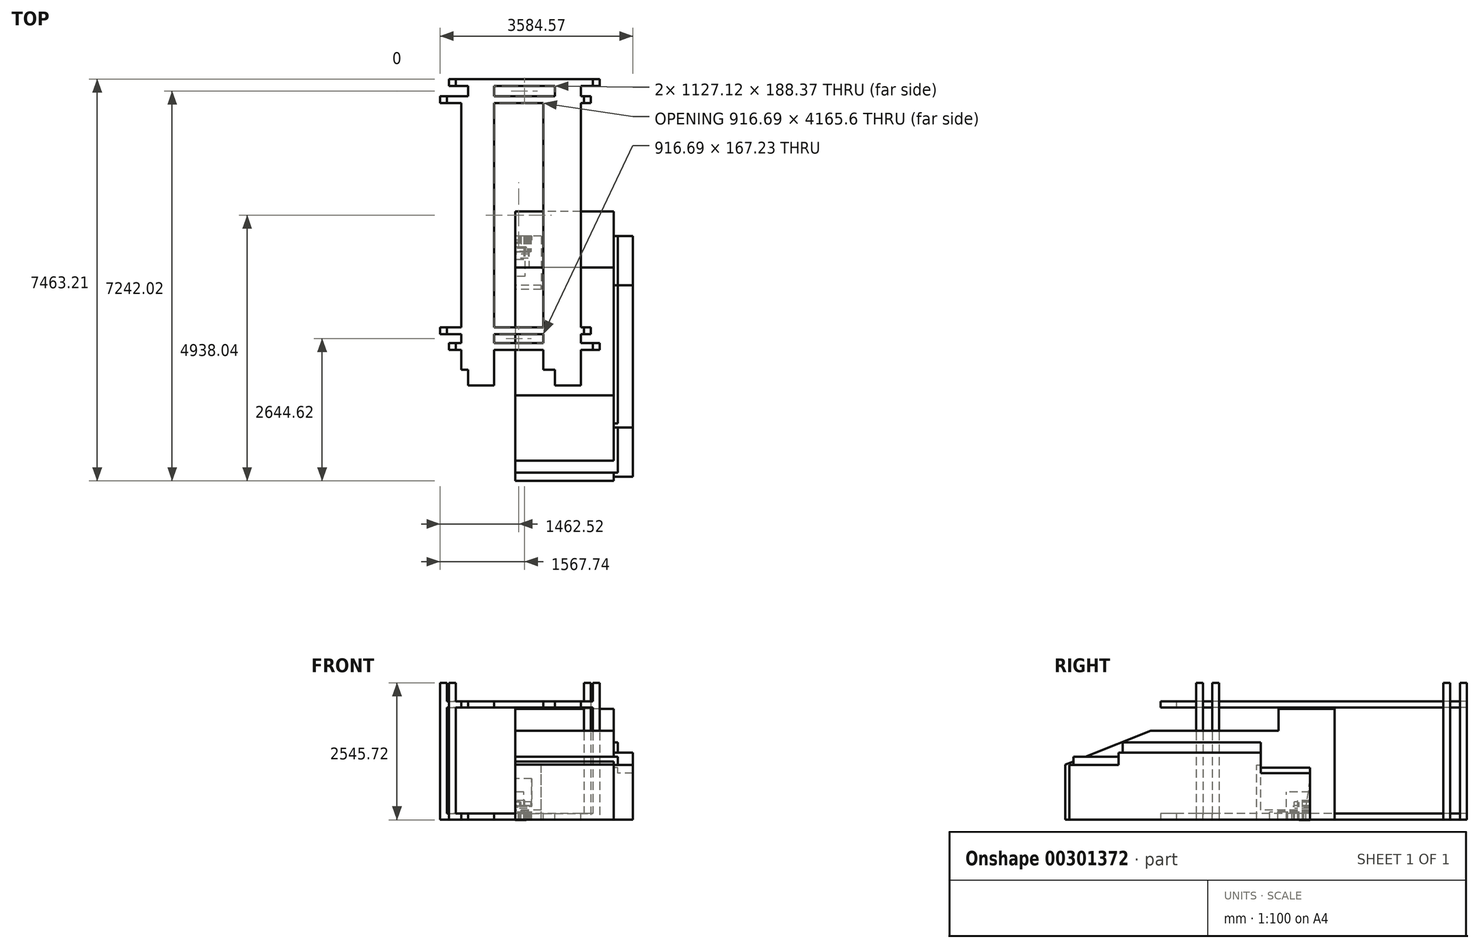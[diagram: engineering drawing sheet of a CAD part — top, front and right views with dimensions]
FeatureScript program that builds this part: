
annotation { "Feature Type Name" : "Feature", "Feature Type Description" : "" }
export const myFeature = defineFeature(function(context is Context, id is Id, definition is map)
    precondition{}
    {
        {
            var Q0;
            Q0=qCreatedBy(makeId("Right.planeOp"),FACE);
            var sketch = newSketch(context, id + "F0", { "sketchPlane" : qUnion([Q0])});
            skLineSegment(sketch, "E0.bottom", {"start": v(0, 0) * mm, "end": v(-4394.2, 0) * mm});
            skLineSegment(sketch, "E0.top", {"start": v(-914.4, 1435.1) * mm, "end": v(-3479.8, 1435.1) * mm});
            skLineSegment(sketch, "E0.left", {"start": v(0, 0) * mm, "end": v(0, 965.2) * mm});
            skLineSegment(sketch, "E0.right", {"start": v(-4394.2, 0) * mm, "end": v(-4394.2, 1168.4) * mm});
            skLineSegment(sketch, "E1", {"start": v(0, 965.2) * mm, "end": v(-914.4, 965.2) * mm});
            skLineSegment(sketch, "E2", {"start": v(-914.4, 965.2) * mm, "end": v(-914.4, 1435.1) * mm});
            skLineSegment(sketch, "E3", {"start": v(-4394.2, 1168.4) * mm, "end": v(-3479.8, 1168.4) * mm});
            skLineSegment(sketch, "E4", {"start": v(-3479.8, 1168.4) * mm, "end": v(-3479.8, 1435.1) * mm});
            skSolve(sketch);
        }
        {
            var Q0;
            Q0=makeQuery(id+"F0.imprint","IMPRINT",FACE,{"disambiguationData":[TD([[makeQuery(id+"F0.imprint","IMPRINT",EDGE,{"derivedFrom":sQuery(id+"F0.wireOp",EDGE,"E0.bottom")}),-1.0]])]});
            extrude(context, id + "F1", {"entities" : qUnion([Q0]), "depth" : 1905 * mm});
        }
        {
            var Q0;
            Q0=qCreatedBy(makeId("Right.planeOp"),FACE);
            var sketch = newSketch(context, id + "F2", { "sketchPlane" : qUnion([Q0])});
            skLineSegment(sketch, "E5.bottom", {"start": v(0, 0) * mm, "end": v(-4470.4, 0) * mm});
            skLineSegment(sketch, "E5.top", {"start": v(-914.4, 1244.6) * mm, "end": v(-3556, 1244.6) * mm});
            skLineSegment(sketch, "E5.left", {"start": v(0, 0) * mm, "end": v(0, 863.6) * mm});
            skLineSegment(sketch, "E5.right", {"start": v(-4470.4, 0) * mm, "end": v(-4470.4, 1016) * mm});
            skLineSegment(sketch, "E6.top", {"start": v(-4470.4, 1016) * mm, "end": v(-3556, 1016) * mm});
            skLineSegment(sketch, "E6.right", {"start": v(-3556, 1244.6) * mm, "end": v(-3556, 1016) * mm});
            skLineSegment(sketch, "E7.top", {"start": v(0, 863.6) * mm, "end": v(-914.4, 863.6) * mm});
            skLineSegment(sketch, "E7.right", {"start": v(-914.4, 1244.6) * mm, "end": v(-914.4, 863.6) * mm});
            skSolve(sketch);
        }
        {
            var Q0;
            Q0 = qSketchRegion(id + "F2", true);
            extrude(context, id + "F3", {"entities" : qUnion([Q0]), "depth" : 2184.4 * mm});
        }
        {
            var Q0;
            Q0=qCreatedBy(makeId("Right.planeOp"),FACE);
            var sketch = newSketch(context, id + "F4", { "sketchPlane" : qUnion([Q0])});
            skLineSegment(sketch, "E8.bottom", {"start": v(0, 0) * mm, "end": v(-990.6, 0) * mm});
            skLineSegment(sketch, "E8.top", {"start": v(0, 177.8) * mm, "end": v(-914.4, 177.8) * mm});
            skLineSegment(sketch, "E8.left", {"start": v(0, 0) * mm, "end": v(0, 177.8) * mm});
            skLineSegment(sketch, "E8.right", {"start": v(-990.6, 0) * mm, "end": v(-990.6, 177.8) * mm});
            skLineSegment(sketch, "E9.top", {"start": v(-990.6, 1016) * mm, "end": v(-914.4, 1016) * mm});
            skLineSegment(sketch, "E9.left", {"start": v(-990.6, 177.8) * mm, "end": v(-990.6, 1016) * mm});
            skLineSegment(sketch, "E9.right", {"start": v(-914.4, 177.8) * mm, "end": v(-914.4, 1016) * mm});
            skSolve(sketch);
        }
        {
            var Q0;
            Q0=makeQuery(id+"F4.imprint","IMPRINT",FACE,{"disambiguationData":[TD([[makeQuery(id+"F4.imprint","IMPRINT",EDGE,{"derivedFrom":sQuery(id+"F4.wireOp",EDGE,"E8.bottom")}),-1.0]])]});
            extrude(context, id + "F5", {"entities" : qUnion([Q0]), "depth" : 482.6 * mm});
        }
        {
            var Q0;
            Q0=qCreatedBy(makeId("Right.planeOp"),FACE);
            var sketch = newSketch(context, id + "F6", { "sketchPlane" : qUnion([Q0])});
            skLineSegment(sketch, "E10.bottom", {"start": v(0, 0) * mm, "end": v(-596.9, 0) * mm});
            skLineSegment(sketch, "E10.top", {"start": v(0, 165.1) * mm, "end": v(-596.9, 165.1) * mm});
            skLineSegment(sketch, "E10.left", {"start": v(0, 0) * mm, "end": v(0, 165.1) * mm});
            skLineSegment(sketch, "E10.right", {"start": v(-596.9, 0) * mm, "end": v(-596.9, 165.1) * mm});
            skSolve(sketch);
        }
        {
            var Q0;
            Q0=makeQuery(id+"F6.imprint","IMPRINT",FACE,{"disambiguationData":[TD([[makeQuery(id+"F6.imprint","IMPRINT",EDGE,{"derivedFrom":sQuery(id+"F6.wireOp",EDGE,"E10.bottom")}),-1.0]])]});
            extrude(context, id + "F7", {"entities" : qUnion([Q0]), "depth" : 254 * mm});
        }
        {
            var Q0;
            Q0=qCreatedBy(makeId("Right.planeOp"),FACE);
            var sketch = newSketch(context, id + "F8", { "sketchPlane" : qUnion([Q0])});
            skLineSegment(sketch, "E11.bottom", {"start": v(0, 0) * mm, "end": v(-228.6, 0) * mm});
            skLineSegment(sketch, "E11.top", {"start": v(0, 355.6) * mm, "end": v(-228.6, 355.6) * mm});
            skLineSegment(sketch, "E11.left", {"start": v(0, 0) * mm, "end": v(0, 355.6) * mm});
            skLineSegment(sketch, "E11.right", {"start": v(-228.6, 0) * mm, "end": v(-228.6, 355.6) * mm});
            skSolve(sketch);
        }
        {
            var Q0;
            Q0 = qSketchRegion(id + "F8", true);
            extrude(context, id + "F9", {"entities" : qUnion([Q0]), "depth" : 177.8 * mm});
        }
        {
            var Q0;
            Q0=qCreatedBy(makeId("Right.planeOp"),FACE);
            var sketch = newSketch(context, id + "F10", { "sketchPlane" : qUnion([Q0])});
            skLineSegment(sketch, "E12.bottom", {"start": v(0, 0) * mm, "end": v(-215.9, 0) * mm});
            skLineSegment(sketch, "E12.top", {"start": v(0, 241.3) * mm, "end": v(-215.9, 241.3) * mm});
            skLineSegment(sketch, "E12.left", {"start": v(0, 0) * mm, "end": v(0, 241.3) * mm});
            skLineSegment(sketch, "E12.right", {"start": v(-215.9, 0) * mm, "end": v(-215.9, 241.3) * mm});
            skSolve(sketch);
        }
        {
            var Q0;
            Q0 = qSketchRegion(id + "F10", true);
            extrude(context, id + "F11", {"entities" : qUnion([Q0]), "depth" : 215.9 * mm});
        }
        {
            var Q0;
            Q0=qCreatedBy(makeId("Right.planeOp"),FACE);
            var sketch = newSketch(context, id + "F12", { "sketchPlane" : qUnion([Q0])});
            skLineSegment(sketch, "E13.bottom", {"start": v(0, 0) * mm, "end": v(-76.2, 0) * mm});
            skLineSegment(sketch, "E13.left", {"start": v(0, 0) * mm, "end": v(0, 762) * mm});
            skLineSegment(sketch, "E13.right", {"start": v(-76.2, 0) * mm, "end": v(-76.2, 254) * mm});
            skLineSegment(sketch, "E14", {"start": v(0, 762) * mm, "end": v(-76.2, 254) * mm});
            skSolve(sketch);
        }
        {
            var Q0;
            Q0 = qSketchRegion(id + "F12", true);
            extrude(context, id + "F13", {"entities" : qUnion([Q0]), "depth" : 304.8 * mm});
        }
        {
            var Q0;
            Q0=qCreatedBy(makeId("Right.planeOp"),FACE);
            var sketch = newSketch(context, id + "F14", { "sketchPlane" : qUnion([Q0])});
            skLineSegment(sketch, "E15.bottom", {"start": v(0, -5.72) * mm, "end": v(-203.2, -5.72) * mm});
            skLineSegment(sketch, "E15.top", {"start": v(0, 133.98) * mm, "end": v(-203.2, 133.98) * mm});
            skLineSegment(sketch, "E15.left", {"start": v(0, -5.72) * mm, "end": v(0, 133.98) * mm});
            skLineSegment(sketch, "E15.right", {"start": v(-203.2, -5.72) * mm, "end": v(-203.2, 133.98) * mm});
            skSolve(sketch);
        }
        {
            var Q0;
            Q0=makeQuery(id+"F14.imprint","IMPRINT",FACE,{"disambiguationData":[TD([[makeQuery(id+"F14.imprint","IMPRINT",EDGE,{"derivedFrom":sQuery(id+"F14.wireOp",EDGE,"E15.bottom")}),-1.0]])]});
            extrude(context, id + "F15", {"entities" : qUnion([Q0]), "depth" : 203.2 * mm});
        }
        {
            var Q0;
            Q0=qCreatedBy(makeId("Right.planeOp"),FACE);
            var sketch = newSketch(context, id + "F16", { "sketchPlane" : qUnion([Q0])});
            skLineSegment(sketch, "E16.bottom", {"start": v(0, 0) * mm, "end": v(-749.3, 0) * mm});
            skLineSegment(sketch, "E16.top", {"start": v(0, 139.7) * mm, "end": v(-749.3, 139.7) * mm});
            skLineSegment(sketch, "E16.left", {"start": v(0, 0) * mm, "end": v(0, 139.7) * mm});
            skLineSegment(sketch, "E16.right", {"start": v(-749.3, 0) * mm, "end": v(-749.3, 139.7) * mm});
            skSolve(sketch);
        }
        {
            var Q0;
            Q0 = qSketchRegion(id + "F16", true);
            extrude(context, id + "F17", {"entities" : qUnion([Q0]), "depth" : 177.8 * mm});
        }
        {
            var Q0;
            Q0=qCreatedBy(makeId("Right.planeOp"),FACE);
            var sketch = newSketch(context, id + "F18", { "sketchPlane" : qUnion([Q0])});
            skLineSegment(sketch, "E17.bottom", {"start": v(0, 0) * mm, "end": v(-336.55, 0) * mm});
            skLineSegment(sketch, "E17.top", {"start": v(0, 114.3) * mm, "end": v(-336.55, 114.3) * mm});
            skLineSegment(sketch, "E17.left", {"start": v(0, 0) * mm, "end": v(0, 114.3) * mm});
            skLineSegment(sketch, "E17.right", {"start": v(-336.55, 0) * mm, "end": v(-336.55, 114.3) * mm});
            skSolve(sketch);
        }
        {
            var Q0;
            Q0 = qSketchRegion(id + "F18", true);
            extrude(context, id + "F19", {"entities" : qUnion([Q0]), "depth" : 254 * mm});
        }
        {
            var Q0;
            Q0=qCreatedBy(makeId("Right.planeOp"),FACE);
            var sketch = newSketch(context, id + "F20", { "sketchPlane" : qUnion([Q0])});
            skLineSegment(sketch, "E18.bottom", {"start": v(0, 0) * mm, "end": v(-285.75, 0) * mm});
            skLineSegment(sketch, "E18.top", {"start": v(0, 209.55) * mm, "end": v(-285.75, 209.55) * mm});
            skLineSegment(sketch, "E18.left", {"start": v(0, 0) * mm, "end": v(0, 209.55) * mm});
            skLineSegment(sketch, "E18.right", {"start": v(-285.75, 0) * mm, "end": v(-285.75, 209.55) * mm});
            skSolve(sketch);
        }
        {
            var Q0;
            Q0 = qSketchRegion(id + "F20", true);
            extrude(context, id + "F21", {"entities" : qUnion([Q0]), "depth" : 222.25 * mm});
        }
        {
            var Q0;
            Q0=qCreatedBy(makeId("Right.planeOp"),FACE);
            var sketch = newSketch(context, id + "F22", { "sketchPlane" : qUnion([Q0])});
            skLineSegment(sketch, "E19.bottom", {"start": v(0, 0) * mm, "end": v(-298.45, 0) * mm});
            skLineSegment(sketch, "E19.top", {"start": v(0, 139.7) * mm, "end": v(-298.45, 139.7) * mm});
            skLineSegment(sketch, "E19.left", {"start": v(0, 0) * mm, "end": v(0, 139.7) * mm});
            skLineSegment(sketch, "E19.right", {"start": v(-298.45, 0) * mm, "end": v(-298.45, 139.7) * mm});
            skSolve(sketch);
        }
        {
            var Q0;
            Q0 = qSketchRegion(id + "F22", true);
            extrude(context, id + "F23", {"entities" : qUnion([Q0]), "depth" : 190.5 * mm});
        }
        {
            var Q0;
            Q0=qCreatedBy(makeId("Right.planeOp"),FACE);
            var sketch = newSketch(context, id + "F24", { "sketchPlane" : qUnion([Q0])});
            skLineSegment(sketch, "E20.bottom", {"start": v(0, 0) * mm, "end": v(-412.75, 0) * mm});
            skLineSegment(sketch, "E20.top", {"start": v(0, 165.1) * mm, "end": v(-412.75, 165.1) * mm});
            skLineSegment(sketch, "E20.left", {"start": v(0, 0) * mm, "end": v(0, 165.1) * mm});
            skLineSegment(sketch, "E20.right", {"start": v(-412.75, 0) * mm, "end": v(-412.75, 165.1) * mm});
            skSolve(sketch);
        }
        {
            var Q0;
            Q0 = qSketchRegion(id + "F24", true);
            extrude(context, id + "F25", {"entities" : qUnion([Q0]), "depth" : 241.3 * mm});
        }
        {
            var Q0;
            Q0=qCreatedBy(makeId("Right.planeOp"),FACE);
            var sketch = newSketch(context, id + "F26", { "sketchPlane" : qUnion([Q0])});
            skLineSegment(sketch, "E21.bottom", {"start": v(0, 0) * mm, "end": v(-139.7, 0) * mm});
            skLineSegment(sketch, "E21.top", {"start": v(0, 336.55) * mm, "end": v(-139.7, 336.55) * mm});
            skLineSegment(sketch, "E21.left", {"start": v(0, 0) * mm, "end": v(0, 336.55) * mm});
            skLineSegment(sketch, "E21.right", {"start": v(-139.7, 0) * mm, "end": v(-139.7, 336.55) * mm});
            skSolve(sketch);
        }
        {
            var Q0;
            Q0 = qSketchRegion(id + "F26", true);
            extrude(context, id + "F27", {"entities" : qUnion([Q0]), "depth" : 82.55 * mm});
        }
        {
            var Q0;
            Q0=qCreatedBy(makeId("Right.planeOp"),FACE);
            var sketch = newSketch(context, id + "F28", { "sketchPlane" : qUnion([Q0])});
            skLineSegment(sketch, "E22.bottom", {"start": v(0, 0) * mm, "end": v(-304.8, 0) * mm});
            skLineSegment(sketch, "E22.top", {"start": v(0, 260.35) * mm, "end": v(-304.8, 260.35) * mm});
            skLineSegment(sketch, "E22.left", {"start": v(0, 0) * mm, "end": v(0, 260.35) * mm});
            skLineSegment(sketch, "E22.right", {"start": v(-304.8, 0) * mm, "end": v(-304.8, 260.35) * mm});
            skSolve(sketch);
        }
        {
            var Q0;
            Q0 = qSketchRegion(id + "F28", true);
            extrude(context, id + "F29", {"entities" : qUnion([Q0]), "depth" : 266.7 * mm});
        }
        {
            var Q0;
            Q0=qCreatedBy(makeId("Right.planeOp"),FACE);
            var sketch = newSketch(context, id + "F30", { "sketchPlane" : qUnion([Q0])});
            skLineSegment(sketch, "E23.bottom", {"start": v(0, 0) * mm, "end": v(-438.15, 0) * mm});
            skLineSegment(sketch, "E23.top", {"start": v(0, 514.35) * mm, "end": v(-438.15, 514.35) * mm});
            skLineSegment(sketch, "E23.left", {"start": v(0, 0) * mm, "end": v(0, 514.35) * mm});
            skLineSegment(sketch, "E23.right", {"start": v(-438.15, 0) * mm, "end": v(-438.15, 514.35) * mm});
            skSolve(sketch);
        }
        {
            var Q0;
            Q0 = qSketchRegion(id + "F30", true);
            extrude(context, id + "F31", {"entities" : qUnion([Q0]), "depth" : 158.75 * mm});
        }
        {
            var Q0;
            Q0=qCreatedBy(makeId("Right.planeOp"),FACE);
            var sketch = newSketch(context, id + "F32", { "sketchPlane" : qUnion([Q0])});
            skLineSegment(sketch, "E24.bottom", {"start": v(0, 0) * mm, "end": v(-203.2, 0) * mm});
            skLineSegment(sketch, "E24.top", {"start": v(0, 323.85) * mm, "end": v(-203.2, 323.85) * mm});
            skLineSegment(sketch, "E24.left", {"start": v(0, 0) * mm, "end": v(0, 323.85) * mm});
            skLineSegment(sketch, "E24.right", {"start": v(-203.2, 0) * mm, "end": v(-203.2, 323.85) * mm});
            skSolve(sketch);
        }
        {
            var Q0;
            Q0 = qSketchRegion(id + "F32", true);
            extrude(context, id + "F33", {"entities" : qUnion([Q0]), "depth" : 107.95 * mm});
        }
        {
            var Q0;
            Q0=qCreatedBy(makeId("Right.planeOp"),FACE);
            var sketch = newSketch(context, id + "F34", { "sketchPlane" : qUnion([Q0])});
            skLineSegment(sketch, "E25.bottom", {"start": v(0, 0) * mm, "end": v(-114.3, 0) * mm});
            skLineSegment(sketch, "E25.top", {"start": v(0, 228.6) * mm, "end": v(-114.3, 228.6) * mm});
            skLineSegment(sketch, "E25.left", {"start": v(0, 0) * mm, "end": v(0, 228.6) * mm});
            skLineSegment(sketch, "E25.right", {"start": v(-114.3, 0) * mm, "end": v(-114.3, 228.6) * mm});
            skSolve(sketch);
        }
        {
            var Q0;
            Q0 = qSketchRegion(id + "F34", true);
            extrude(context, id + "F35", {"entities" : qUnion([Q0]), "depth" : 57.15 * mm});
        }
        {
            var Q0;
            Q0=qCreatedBy(makeId("Right.planeOp"),FACE);
            var sketch = newSketch(context, id + "F36", { "sketchPlane" : qUnion([Q0])});
            skLineSegment(sketch, "E26.bottom", {"start": v(0, 0) * mm, "end": v(-292.1, 0) * mm});
            skLineSegment(sketch, "E26.top", {"start": v(0, 330.2) * mm, "end": v(-292.1, 330.2) * mm});
            skLineSegment(sketch, "E26.left", {"start": v(0, 0) * mm, "end": v(0, 330.2) * mm});
            skLineSegment(sketch, "E26.right", {"start": v(-292.1, 0) * mm, "end": v(-292.1, 330.2) * mm});
            skSolve(sketch);
        }
        {
            var Q0;
            Q0 = qSketchRegion(id + "F36", true);
            extrude(context, id + "F37", {"entities" : qUnion([Q0]), "depth" : 292.1 * mm});
        }
        {
            var Q0;
            Q0=qCreatedBy(makeId("Right.planeOp"),FACE);
            var sketch = newSketch(context, id + "F38", { "sketchPlane" : qUnion([Q0])});
            skLineSegment(sketch, "E27.bottom", {"start": v(0, 0) * mm, "end": v(-4546.6, 0) * mm});
            skLineSegment(sketch, "E27.top", {"start": v(-583.6, 1651) * mm, "end": v(-2956.24, 1651) * mm});
            skLineSegment(sketch, "E27.left", {"start": v(0, 0) * mm, "end": v(0, 825.5) * mm});
            skLineSegment(sketch, "E27.right", {"start": v(-4546.6, 0) * mm, "end": v(-4546.6, 1018.82) * mm});
            skLineSegment(sketch, "E28", {"start": v(-2956.24, 1651) * mm, "end": v(-4546.6, 1018.82) * mm});
            skLineSegment(sketch, "E29", {"start": v(-583.6, 1651) * mm, "end": v(0, 825.5) * mm});
            skPoint(sketch, "E30.orphan", {"position": v(0, 1651) * mm});
            skLineSegment(sketch, "E31", {"start": v(-583.6, 2057.4) * mm, "end": v(457.2, 2057.4) * mm});
            skLineSegment(sketch, "E32", {"start": v(457.2, 0) * mm, "end": v(457.2, 2057.4) * mm});
            skLineSegment(sketch, "E33", {"start": v(-583.6, 1651) * mm, "end": v(-583.6, 2057.4) * mm});
            skLineSegment(sketch, "E34", {"start": v(457.2, 0) * mm, "end": v(0, 0) * mm});
            skSolve(sketch);
        }
        {
            var Q0;
            Q0 = qSketchRegion(id + "F38", true);
            extrude(context, id + "F39", {"entities" : qUnion([Q0]), "depth" : 1828.8 * mm});
        }
        {
            var Q0;
            Q0=qCreatedBy(makeId("Top.planeOp"),FACE);
            var sketch = newSketch(context, id + "F40", { "sketchPlane" : qUnion([Q0])});
            skLineSegment(sketch, "E35.bottom", {"start": v(1440.75, 2916.6) * mm, "end": v(1567.75, 2916.6) * mm});
            skLineSegment(sketch, "E35.top", {"start": v(1440.75, 2789.6) * mm, "end": v(1567.75, 2789.6) * mm});
            skLineSegment(sketch, "E35.left", {"start": v(1440.75, 2916.6) * mm, "end": v(1440.75, 2789.6) * mm});
            skLineSegment(sketch, "E35.right", {"start": v(1567.75, 2916.6) * mm, "end": v(1567.75, 2789.6) * mm});
            skLineSegment(sketch, "E36.bottom", {"start": v(1567.75, -1985.6) * mm, "end": v(1440.75, -1985.6) * mm});
            skLineSegment(sketch, "E36.top", {"start": v(1567.75, -2112.6) * mm, "end": v(1440.75, -2112.6) * mm});
            skLineSegment(sketch, "E36.left", {"start": v(1567.75, -1985.6) * mm, "end": v(1567.75, -2112.6) * mm});
            skLineSegment(sketch, "E36.right", {"start": v(1440.75, -1985.6) * mm, "end": v(1440.75, -2112.6) * mm});
            skLineSegment(sketch, "E37", {"start": v(167.57, 3036.9) * mm, "end": v(167.57, -1974.98) * mm, "construction": true});
            skLineSegment(sketch, "E38.bottom", {"start": v(1213.73, 2916.6) * mm, "end": v(731.13, 2916.6) * mm});
            skLineSegment(sketch, "E38.top", {"start": v(1213.73, -2773) * mm, "end": v(731.13, -2773) * mm});
            skLineSegment(sketch, "E38.left", {"start": v(1213.73, 2916.6) * mm, "end": v(1213.73, -2773) * mm});
            skLineSegment(sketch, "E38.right", {"start": v(731.13, 2916.6) * mm, "end": v(731.13, -2773) * mm});
            skLineSegment(sketch, "E39.MirrorCS", {"start": v(-878.6, -2773) * mm, "end": v(-396, -2773) * mm});
            skLineSegment(sketch, "E40.MirrorCS", {"start": v(-396, 2916.6) * mm, "end": v(-396, -2773) * mm});
            skLineSegment(sketch, "E41.MirrorCS", {"start": v(-878.6, 2916.6) * mm, "end": v(-878.6, -2773) * mm});
            skLineSegment(sketch, "E42.MirrorCS", {"start": v(-878.6, 2916.6) * mm, "end": v(-396, 2916.6) * mm});
            skLineSegment(sketch, "E43.MirrorCS", {"start": v(-1105.6, 2916.6) * mm, "end": v(-1105.6, 2789.6) * mm});
            skLineSegment(sketch, "E44.MirrorCS", {"start": v(-1232.6, 2916.6) * mm, "end": v(-1232.6, 2789.6) * mm});
            skLineSegment(sketch, "E45.MirrorCS", {"start": v(-1105.6, 2789.6) * mm, "end": v(-1232.6, 2789.6) * mm});
            skLineSegment(sketch, "E46.MirrorCS", {"start": v(-1105.6, 2916.6) * mm, "end": v(-1232.6, 2916.6) * mm});
            skLineSegment(sketch, "E47.MirrorCS", {"start": v(-1232.6, -1985.6) * mm, "end": v(-1232.6, -2112.6) * mm});
            skLineSegment(sketch, "E48.MirrorCS", {"start": v(-1232.6, -1985.6) * mm, "end": v(-1105.6, -1985.6) * mm});
            skLineSegment(sketch, "E49.MirrorCS", {"start": v(-1105.6, -1985.6) * mm, "end": v(-1105.6, -2112.6) * mm});
            skLineSegment(sketch, "E50.MirrorCS", {"start": v(-1232.6, -2112.6) * mm, "end": v(-1105.6, -2112.6) * mm});
            skLineSegment(sketch, "E51", {"start": v(-1105.6, 2916.6) * mm, "end": v(1440.75, 2916.6) * mm});
            skLineSegment(sketch, "E52", {"start": v(1440.75, 2789.6) * mm, "end": v(-1105.6, 2789.6) * mm});
            skLineSegment(sketch, "E53", {"start": v(1440.75, -1985.6) * mm, "end": v(-1105.6, -1985.6) * mm});
            skLineSegment(sketch, "E54", {"start": v(-1105.6, -2112.6) * mm, "end": v(1440.75, -2112.6) * mm});
            skSolve(sketch);
        }
        {
            var Q0;
            {var subQ0=sQuery(id+"F40.wireOp",EDGE,"E36.right");Q0=makeQuery(id+"F40.imprint","IMPRINT",FACE,{"disambiguationData":[TD([[makeQuery(id+"F40.imprint","IMPRINT",EDGE,{"derivedFrom":subQ0}),-1.0]])]});}
            var Q1;
            {var subQ0=sQuery(id+"F40.wireOp",EDGE,"E53");var subQ1=sQuery(id+"F40.wireOp",EDGE,"E38.left");var subQ2=makeQuery(id+"F40.imprint","INTERSECT",VERTEX,{"derivedFrom":[subQ1,subQ0]});Q1=makeQuery(id+"F40.imprint","IMPRINT",FACE,{"disambiguationData":[TD([[makeQuery(id+"F40.imprint","IMPRINT",EDGE,{"disambiguationData":[TD([[subQ2,-1.0]])],"derivedFrom":subQ1}),-1.0]])]});}
            var Q2;
            {var subQ0=sQuery(id+"F40.wireOp",EDGE,"E54");var subQ1=sQuery(id+"F40.wireOp",EDGE,"E38.right");var subQ2=makeQuery(id+"F40.imprint","INTERSECT",VERTEX,{"derivedFrom":[subQ1,subQ0]});Q2=makeQuery(id+"F40.imprint","IMPRINT",FACE,{"disambiguationData":[TD([[makeQuery(id+"F40.imprint","IMPRINT",EDGE,{"disambiguationData":[TD([[subQ2,1.0]])],"derivedFrom":subQ1}),-1.0]])]});}
            var Q3;
            {var subQ0=sQuery(id+"F40.wireOp",EDGE,"E54");var subQ1=sQuery(id+"F40.wireOp",EDGE,"E40.MirrorCS");var subQ2=makeQuery(id+"F40.imprint","INTERSECT",VERTEX,{"derivedFrom":[subQ1,subQ0]});Q3=makeQuery(id+"F40.imprint","IMPRINT",FACE,{"disambiguationData":[TD([[makeQuery(id+"F40.imprint","IMPRINT",EDGE,{"disambiguationData":[TD([[subQ2,1.0]])],"derivedFrom":subQ1}),-1.0]])]});}
            var Q4;
            {var subQ5=sQuery(id+"F40.wireOp",EDGE,"E49.MirrorCS");Q4=makeQuery(id+"F40.imprint","IMPRINT",FACE,{"disambiguationData":[TD([[makeQuery(id+"F40.imprint","IMPRINT",EDGE,{"derivedFrom":subQ5}),1.0]])]});}
            var Q5;
            {var subQ0=sQuery(id+"F40.wireOp",EDGE,"E52");var subQ1=sQuery(id+"F40.wireOp",EDGE,"E40.MirrorCS");var subQ2=makeQuery(id+"F40.imprint","INTERSECT",VERTEX,{"derivedFrom":[subQ1,subQ0]});Q5=makeQuery(id+"F40.imprint","IMPRINT",FACE,{"disambiguationData":[TD([[makeQuery(id+"F40.imprint","IMPRINT",EDGE,{"disambiguationData":[TD([[subQ2,-1.0]])],"derivedFrom":subQ1}),-1.0]])]});}
            var Q6;
            {var subQ0=sQuery(id+"F40.wireOp",EDGE,"E39.MirrorCS");Q6=makeQuery(id+"F40.imprint","IMPRINT",FACE,{"disambiguationData":[TD([[makeQuery(id+"F40.imprint","IMPRINT",EDGE,{"derivedFrom":subQ0}),1.0]])]});}
            var Q7;
            {var subQ0=sQuery(id+"F40.wireOp",EDGE,"E38.top");Q7=makeQuery(id+"F40.imprint","IMPRINT",FACE,{"disambiguationData":[TD([[makeQuery(id+"F40.imprint","IMPRINT",EDGE,{"derivedFrom":subQ0}),-1.0]])]});}
            var Q8;
            {var subQ0=sQuery(id+"F40.wireOp",EDGE,"E52");var subQ1=sQuery(id+"F40.wireOp",EDGE,"E38.left");var subQ2=makeQuery(id+"F40.imprint","INTERSECT",VERTEX,{"derivedFrom":[subQ1,subQ0]});Q8=makeQuery(id+"F40.imprint","IMPRINT",FACE,{"disambiguationData":[TD([[makeQuery(id+"F40.imprint","IMPRINT",EDGE,{"disambiguationData":[TD([[subQ2,-1.0]])],"derivedFrom":subQ1}),-1.0]])]});}
            var Q9;
            {var subQ0=sQuery(id+"F40.wireOp",EDGE,"E35.left");Q9=makeQuery(id+"F40.imprint","IMPRINT",FACE,{"disambiguationData":[TD([[makeQuery(id+"F40.imprint","IMPRINT",EDGE,{"derivedFrom":subQ0}),-1.0]])]});}
            var Q10;
            {var subQ0=sQuery(id+"F40.wireOp",EDGE,"E51");var subQ1=sQuery(id+"F40.wireOp",EDGE,"E38.left");var subQ2=makeQuery(id+"F40.imprint","INTERSECT",VERTEX,{"derivedFrom":[subQ1,subQ0]});Q10=makeQuery(id+"F40.imprint","IMPRINT",FACE,{"disambiguationData":[TD([[makeQuery(id+"F40.imprint","IMPRINT",EDGE,{"disambiguationData":[TD([[subQ2,-1.0]])],"derivedFrom":subQ1}),-1.0]])]});}
            var Q11;
            {var subQ0=sQuery(id+"F40.wireOp",EDGE,"E51");var subQ1=sQuery(id+"F40.wireOp",EDGE,"E38.right");var subQ2=makeQuery(id+"F40.imprint","INTERSECT",VERTEX,{"derivedFrom":[subQ1,subQ0]});Q11=makeQuery(id+"F40.imprint","IMPRINT",FACE,{"disambiguationData":[TD([[makeQuery(id+"F40.imprint","IMPRINT",EDGE,{"disambiguationData":[TD([[subQ2,-1.0]])],"derivedFrom":subQ1}),-1.0]])]});}
            var Q12;
            {var subQ0=sQuery(id+"F40.wireOp",EDGE,"E51");var subQ1=sQuery(id+"F40.wireOp",EDGE,"E40.MirrorCS");var subQ2=makeQuery(id+"F40.imprint","INTERSECT",VERTEX,{"derivedFrom":[subQ1,subQ0]});Q12=makeQuery(id+"F40.imprint","IMPRINT",FACE,{"disambiguationData":[TD([[makeQuery(id+"F40.imprint","IMPRINT",EDGE,{"disambiguationData":[TD([[subQ2,-1.0]])],"derivedFrom":subQ1}),-1.0]])]});}
            var Q13;
            {var subQ5=sQuery(id+"F40.wireOp",EDGE,"E43.MirrorCS");Q13=makeQuery(id+"F40.imprint","IMPRINT",FACE,{"disambiguationData":[TD([[makeQuery(id+"F40.imprint","IMPRINT",EDGE,{"derivedFrom":subQ5}),1.0]])]});}
            extrude(context, id + "F41", {"entities" : qUnion([Q0, Q1, Q2, Q3, Q4, Q5, Q6, Q7, Q8, Q9, Q10, Q11, Q12, Q13]), "depth" : 2197.1 * mm, "hasSecondDirection" : true, "secondDirectionOppositeDirection" : false, "secondDirectionDepth" : 2082.8 * mm});
        }
        {
            var Q0;
            Q0=makeQuery(id+"F40.imprint","IMPRINT",FACE,{"disambiguationData":[TD([[makeQuery(id+"F40.imprint","IMPRINT",EDGE,{"derivedFrom":sQuery(id+"F40.wireOp",EDGE,"E47.MirrorCS")}),1.0]])]});
            var Q1;
            Q1=makeQuery(id+"F40.imprint","IMPRINT",FACE,{"disambiguationData":[TD([[makeQuery(id+"F40.imprint","IMPRINT",EDGE,{"derivedFrom":sQuery(id+"F40.wireOp",EDGE,"E36.bottom")}),1.0]])]});
            var Q2;
            Q2=makeQuery(id+"F40.imprint","IMPRINT",FACE,{"disambiguationData":[TD([[makeQuery(id+"F40.imprint","IMPRINT",EDGE,{"derivedFrom":sQuery(id+"F40.wireOp",EDGE,"E35.bottom")}),-1.0]])]});
            var Q3;
            Q3=makeQuery(id+"F40.imprint","IMPRINT",FACE,{"disambiguationData":[TD([[makeQuery(id+"F40.imprint","IMPRINT",EDGE,{"derivedFrom":sQuery(id+"F40.wireOp",EDGE,"E43.MirrorCS")}),-1.0]])]});
            extrude(context, id + "F42", {"entities" : qUnion([Q0, Q1, Q2, Q3]), "operationType" : NewBodyOperationType.ADD, "depth" : 2540 * mm});
        }
        {
            var Q0;
            {var subQ5=sQuery(id+"F40.wireOp",EDGE,"E49.MirrorCS");Q0=makeQuery(id+"F40.imprint","IMPRINT",FACE,{"disambiguationData":[TD([[makeQuery(id+"F40.imprint","IMPRINT",EDGE,{"derivedFrom":subQ5}),1.0]])]});}
            var Q1;
            {var subQ0=sQuery(id+"F40.wireOp",EDGE,"E39.MirrorCS");Q1=makeQuery(id+"F40.imprint","IMPRINT",FACE,{"disambiguationData":[TD([[makeQuery(id+"F40.imprint","IMPRINT",EDGE,{"derivedFrom":subQ0}),1.0]])]});}
            var Q2;
            {var subQ0=sQuery(id+"F40.wireOp",EDGE,"E54");var subQ1=sQuery(id+"F40.wireOp",EDGE,"E40.MirrorCS");var subQ2=makeQuery(id+"F40.imprint","INTERSECT",VERTEX,{"derivedFrom":[subQ1,subQ0]});Q2=makeQuery(id+"F40.imprint","IMPRINT",FACE,{"disambiguationData":[TD([[makeQuery(id+"F40.imprint","IMPRINT",EDGE,{"disambiguationData":[TD([[subQ2,1.0]])],"derivedFrom":subQ1}),-1.0]])]});}
            var Q3;
            {var subQ0=sQuery(id+"F40.wireOp",EDGE,"E52");var subQ1=sQuery(id+"F40.wireOp",EDGE,"E40.MirrorCS");var subQ2=makeQuery(id+"F40.imprint","INTERSECT",VERTEX,{"derivedFrom":[subQ1,subQ0]});Q3=makeQuery(id+"F40.imprint","IMPRINT",FACE,{"disambiguationData":[TD([[makeQuery(id+"F40.imprint","IMPRINT",EDGE,{"disambiguationData":[TD([[subQ2,-1.0]])],"derivedFrom":subQ1}),-1.0]])]});}
            var Q4;
            {var subQ0=sQuery(id+"F40.wireOp",EDGE,"E54");var subQ1=sQuery(id+"F40.wireOp",EDGE,"E38.right");var subQ2=makeQuery(id+"F40.imprint","INTERSECT",VERTEX,{"derivedFrom":[subQ1,subQ0]});Q4=makeQuery(id+"F40.imprint","IMPRINT",FACE,{"disambiguationData":[TD([[makeQuery(id+"F40.imprint","IMPRINT",EDGE,{"disambiguationData":[TD([[subQ2,1.0]])],"derivedFrom":subQ1}),-1.0]])]});}
            var Q5;
            {var subQ0=sQuery(id+"F40.wireOp",EDGE,"E38.top");Q5=makeQuery(id+"F40.imprint","IMPRINT",FACE,{"disambiguationData":[TD([[makeQuery(id+"F40.imprint","IMPRINT",EDGE,{"derivedFrom":subQ0}),-1.0]])]});}
            var Q6;
            {var subQ0=sQuery(id+"F40.wireOp",EDGE,"E53");var subQ1=sQuery(id+"F40.wireOp",EDGE,"E38.left");var subQ2=makeQuery(id+"F40.imprint","INTERSECT",VERTEX,{"derivedFrom":[subQ1,subQ0]});Q6=makeQuery(id+"F40.imprint","IMPRINT",FACE,{"disambiguationData":[TD([[makeQuery(id+"F40.imprint","IMPRINT",EDGE,{"disambiguationData":[TD([[subQ2,-1.0]])],"derivedFrom":subQ1}),-1.0]])]});}
            var Q7;
            {var subQ0=sQuery(id+"F40.wireOp",EDGE,"E36.right");Q7=makeQuery(id+"F40.imprint","IMPRINT",FACE,{"disambiguationData":[TD([[makeQuery(id+"F40.imprint","IMPRINT",EDGE,{"derivedFrom":subQ0}),-1.0]])]});}
            var Q8;
            {var subQ0=sQuery(id+"F40.wireOp",EDGE,"E52");var subQ1=sQuery(id+"F40.wireOp",EDGE,"E38.left");var subQ2=makeQuery(id+"F40.imprint","INTERSECT",VERTEX,{"derivedFrom":[subQ1,subQ0]});Q8=makeQuery(id+"F40.imprint","IMPRINT",FACE,{"disambiguationData":[TD([[makeQuery(id+"F40.imprint","IMPRINT",EDGE,{"disambiguationData":[TD([[subQ2,-1.0]])],"derivedFrom":subQ1}),-1.0]])]});}
            var Q9;
            {var subQ0=sQuery(id+"F40.wireOp",EDGE,"E35.left");Q9=makeQuery(id+"F40.imprint","IMPRINT",FACE,{"disambiguationData":[TD([[makeQuery(id+"F40.imprint","IMPRINT",EDGE,{"derivedFrom":subQ0}),-1.0]])]});}
            var Q10;
            {var subQ0=sQuery(id+"F40.wireOp",EDGE,"E51");var subQ1=sQuery(id+"F40.wireOp",EDGE,"E38.left");var subQ2=makeQuery(id+"F40.imprint","INTERSECT",VERTEX,{"derivedFrom":[subQ1,subQ0]});Q10=makeQuery(id+"F40.imprint","IMPRINT",FACE,{"disambiguationData":[TD([[makeQuery(id+"F40.imprint","IMPRINT",EDGE,{"disambiguationData":[TD([[subQ2,-1.0]])],"derivedFrom":subQ1}),-1.0]])]});}
            var Q11;
            {var subQ0=sQuery(id+"F40.wireOp",EDGE,"E51");var subQ1=sQuery(id+"F40.wireOp",EDGE,"E38.right");var subQ2=makeQuery(id+"F40.imprint","INTERSECT",VERTEX,{"derivedFrom":[subQ1,subQ0]});Q11=makeQuery(id+"F40.imprint","IMPRINT",FACE,{"disambiguationData":[TD([[makeQuery(id+"F40.imprint","IMPRINT",EDGE,{"disambiguationData":[TD([[subQ2,-1.0]])],"derivedFrom":subQ1}),-1.0]])]});}
            var Q12;
            {var subQ0=sQuery(id+"F40.wireOp",EDGE,"E51");var subQ1=sQuery(id+"F40.wireOp",EDGE,"E40.MirrorCS");var subQ2=makeQuery(id+"F40.imprint","INTERSECT",VERTEX,{"derivedFrom":[subQ1,subQ0]});Q12=makeQuery(id+"F40.imprint","IMPRINT",FACE,{"disambiguationData":[TD([[makeQuery(id+"F40.imprint","IMPRINT",EDGE,{"disambiguationData":[TD([[subQ2,-1.0]])],"derivedFrom":subQ1}),-1.0]])]});}
            var Q13;
            {var subQ5=sQuery(id+"F40.wireOp",EDGE,"E43.MirrorCS");Q13=makeQuery(id+"F40.imprint","IMPRINT",FACE,{"disambiguationData":[TD([[makeQuery(id+"F40.imprint","IMPRINT",EDGE,{"derivedFrom":subQ5}),1.0]])]});}
            extrude(context, id + "F43", {"entities" : qUnion([Q0, Q1, Q2, Q3, Q4, Q5, Q6, Q7, Q8, Q9, Q10, Q11, Q12, Q13]), "operationType" : NewBodyOperationType.ADD, "depth" : 114.3 * mm, "offsetDistance" : 25.4 * mm});
        }
        {
            var Q0;
            Q0=qCreatedBy(makeId("Top.planeOp"),FACE);
            var sketch = newSketch(context, id + "F44", { "sketchPlane" : qUnion([Q0])});
            skLineSegment(sketch, "E55.bottom", {"start": v(1273.17, 2601.24) * mm, "end": v(1400.17, 2601.24) * mm});
            skLineSegment(sketch, "E55.top", {"start": v(1273.18, 2474.24) * mm, "end": v(1400.17, 2474.24) * mm});
            skLineSegment(sketch, "E55.left", {"start": v(1273.18, 2601.24) * mm, "end": v(1273.18, 2474.24) * mm});
            skLineSegment(sketch, "E55.right", {"start": v(1400.17, 2601.24) * mm, "end": v(1400.17, 2474.24) * mm});
            skLineSegment(sketch, "E56.bottom", {"start": v(1400.17, -1691.36) * mm, "end": v(1273.17, -1691.36) * mm});
            skLineSegment(sketch, "E56.top", {"start": v(1400.17, -1818.36) * mm, "end": v(1273.17, -1818.36) * mm});
            skLineSegment(sketch, "E56.left", {"start": v(1400.17, -1691.36) * mm, "end": v(1400.17, -1818.36) * mm});
            skLineSegment(sketch, "E56.right", {"start": v(1273.17, -1691.36) * mm, "end": v(1273.17, -1818.36) * mm});
            skLineSegment(sketch, "E57", {"start": v(0, 2721.54) * mm, "end": v(0, -2290.34) * mm, "construction": true});
            skLineSegment(sketch, "E58.bottom", {"start": v(1003.3, 2601.24) * mm, "end": v(520.7, 2601.24) * mm});
            skLineSegment(sketch, "E58.top", {"start": v(1003.3, -2478.76) * mm, "end": v(520.7, -2478.76) * mm});
            skLineSegment(sketch, "E58.left", {"start": v(1003.3, 2601.24) * mm, "end": v(1003.3, -2478.76) * mm});
            skLineSegment(sketch, "E58.right", {"start": v(520.7, 2601.24) * mm, "end": v(520.7, -2478.76) * mm});
            skLineSegment(sketch, "E59.MirrorCS", {"start": v(-1003.3, -2478.76) * mm, "end": v(-520.7, -2478.76) * mm});
            skLineSegment(sketch, "E60.MirrorCS", {"start": v(-520.7, 2601.24) * mm, "end": v(-520.7, -2478.76) * mm});
            skLineSegment(sketch, "E61.MirrorCS", {"start": v(-1003.3, 2601.24) * mm, "end": v(-1003.3, -2478.76) * mm});
            skLineSegment(sketch, "E62.MirrorCS", {"start": v(-1003.3, 2601.24) * mm, "end": v(-520.7, 2601.24) * mm});
            skLineSegment(sketch, "E63.MirrorCS", {"start": v(-1273.18, 2601.24) * mm, "end": v(-1273.18, 2474.24) * mm});
            skLineSegment(sketch, "E64.MirrorCS", {"start": v(-1400.18, 2601.24) * mm, "end": v(-1400.18, 2474.24) * mm});
            skLineSegment(sketch, "E65.MirrorCS", {"start": v(-1273.18, 2474.24) * mm, "end": v(-1400.18, 2474.24) * mm});
            skLineSegment(sketch, "E66.MirrorCS", {"start": v(-1273.18, 2601.24) * mm, "end": v(-1400.18, 2601.24) * mm});
            skLineSegment(sketch, "E67.MirrorCS", {"start": v(-1400.17, -1691.36) * mm, "end": v(-1400.17, -1818.36) * mm});
            skLineSegment(sketch, "E68.MirrorCS", {"start": v(-1400.17, -1691.36) * mm, "end": v(-1273.17, -1691.36) * mm});
            skLineSegment(sketch, "E69.MirrorCS", {"start": v(-1273.17, -1691.36) * mm, "end": v(-1273.17, -1818.36) * mm});
            skLineSegment(sketch, "E70.MirrorCS", {"start": v(-1400.17, -1818.36) * mm, "end": v(-1273.17, -1818.36) * mm});
            skLineSegment(sketch, "E71", {"start": v(-1273.18, 2601.24) * mm, "end": v(1273.17, 2601.24) * mm});
            skLineSegment(sketch, "E72", {"start": v(1273.18, 2474.24) * mm, "end": v(-1273.18, 2474.24) * mm});
            skLineSegment(sketch, "E73", {"start": v(1273.17, -1691.36) * mm, "end": v(-1273.17, -1691.36) * mm});
            skLineSegment(sketch, "E74", {"start": v(-1273.17, -1818.36) * mm, "end": v(1273.17, -1818.36) * mm});
            skSolve(sketch);
        }
        {
            var Q0;
            {var subQ5=sQuery(id+"F44.wireOp",EDGE,"E69.MirrorCS");Q0=makeQuery(id+"F44.imprint","IMPRINT",FACE,{"disambiguationData":[TD([[makeQuery(id+"F44.imprint","IMPRINT",EDGE,{"derivedFrom":subQ5}),1.0]])]});}
            var Q1;
            {var subQ0=sQuery(id+"F44.wireOp",EDGE,"E74");var subQ1=sQuery(id+"F44.wireOp",EDGE,"E60.MirrorCS");var subQ2=makeQuery(id+"F44.imprint","INTERSECT",VERTEX,{"derivedFrom":[subQ1,subQ0]});Q1=makeQuery(id+"F44.imprint","IMPRINT",FACE,{"disambiguationData":[TD([[makeQuery(id+"F44.imprint","IMPRINT",EDGE,{"disambiguationData":[TD([[subQ2,1.0]])],"derivedFrom":subQ1}),-1.0]])]});}
            var Q2;
            {var subQ0=sQuery(id+"F44.wireOp",EDGE,"E59.MirrorCS");Q2=makeQuery(id+"F44.imprint","IMPRINT",FACE,{"disambiguationData":[TD([[makeQuery(id+"F44.imprint","IMPRINT",EDGE,{"derivedFrom":subQ0}),1.0]])]});}
            var Q3;
            {var subQ0=sQuery(id+"F44.wireOp",EDGE,"E72");var subQ1=sQuery(id+"F44.wireOp",EDGE,"E60.MirrorCS");var subQ2=makeQuery(id+"F44.imprint","INTERSECT",VERTEX,{"derivedFrom":[subQ1,subQ0]});Q3=makeQuery(id+"F44.imprint","IMPRINT",FACE,{"disambiguationData":[TD([[makeQuery(id+"F44.imprint","IMPRINT",EDGE,{"disambiguationData":[TD([[subQ2,-1.0]])],"derivedFrom":subQ1}),-1.0]])]});}
            var Q4;
            {var subQ0=sQuery(id+"F44.wireOp",EDGE,"E74");var subQ1=sQuery(id+"F44.wireOp",EDGE,"E58.right");var subQ2=makeQuery(id+"F44.imprint","INTERSECT",VERTEX,{"derivedFrom":[subQ1,subQ0]});Q4=makeQuery(id+"F44.imprint","IMPRINT",FACE,{"disambiguationData":[TD([[makeQuery(id+"F44.imprint","IMPRINT",EDGE,{"disambiguationData":[TD([[subQ2,1.0]])],"derivedFrom":subQ1}),-1.0]])]});}
            var Q5;
            {var subQ0=sQuery(id+"F44.wireOp",EDGE,"E58.top");Q5=makeQuery(id+"F44.imprint","IMPRINT",FACE,{"disambiguationData":[TD([[makeQuery(id+"F44.imprint","IMPRINT",EDGE,{"derivedFrom":subQ0}),-1.0]])]});}
            var Q6;
            {var subQ0=sQuery(id+"F44.wireOp",EDGE,"E73");var subQ1=sQuery(id+"F44.wireOp",EDGE,"E58.left");var subQ2=makeQuery(id+"F44.imprint","INTERSECT",VERTEX,{"derivedFrom":[subQ1,subQ0]});Q6=makeQuery(id+"F44.imprint","IMPRINT",FACE,{"disambiguationData":[TD([[makeQuery(id+"F44.imprint","IMPRINT",EDGE,{"disambiguationData":[TD([[subQ2,-1.0]])],"derivedFrom":subQ1}),-1.0]])]});}
            var Q7;
            {var subQ0=sQuery(id+"F44.wireOp",EDGE,"E56.right");Q7=makeQuery(id+"F44.imprint","IMPRINT",FACE,{"disambiguationData":[TD([[makeQuery(id+"F44.imprint","IMPRINT",EDGE,{"derivedFrom":subQ0}),-1.0]])]});}
            var Q8;
            {var subQ0=sQuery(id+"F44.wireOp",EDGE,"E72");var subQ1=sQuery(id+"F44.wireOp",EDGE,"E58.left");var subQ2=makeQuery(id+"F44.imprint","INTERSECT",VERTEX,{"derivedFrom":[subQ1,subQ0]});Q8=makeQuery(id+"F44.imprint","IMPRINT",FACE,{"disambiguationData":[TD([[makeQuery(id+"F44.imprint","IMPRINT",EDGE,{"disambiguationData":[TD([[subQ2,-1.0]])],"derivedFrom":subQ1}),-1.0]])]});}
            var Q9;
            {var subQ0=sQuery(id+"F44.wireOp",EDGE,"E55.left");Q9=makeQuery(id+"F44.imprint","IMPRINT",FACE,{"disambiguationData":[TD([[makeQuery(id+"F44.imprint","IMPRINT",EDGE,{"derivedFrom":subQ0}),-1.0]])]});}
            var Q10;
            {var subQ0=sQuery(id+"F44.wireOp",EDGE,"E71");var subQ1=sQuery(id+"F44.wireOp",EDGE,"E58.left");var subQ2=makeQuery(id+"F44.imprint","INTERSECT",VERTEX,{"derivedFrom":[subQ1,subQ0]});Q10=makeQuery(id+"F44.imprint","IMPRINT",FACE,{"disambiguationData":[TD([[makeQuery(id+"F44.imprint","IMPRINT",EDGE,{"disambiguationData":[TD([[subQ2,-1.0]])],"derivedFrom":subQ1}),-1.0]])]});}
            var Q11;
            {var subQ0=sQuery(id+"F44.wireOp",EDGE,"E71");var subQ1=sQuery(id+"F44.wireOp",EDGE,"E58.right");var subQ2=makeQuery(id+"F44.imprint","INTERSECT",VERTEX,{"derivedFrom":[subQ1,subQ0]});Q11=makeQuery(id+"F44.imprint","IMPRINT",FACE,{"disambiguationData":[TD([[makeQuery(id+"F44.imprint","IMPRINT",EDGE,{"disambiguationData":[TD([[subQ2,-1.0]])],"derivedFrom":subQ1}),-1.0]])]});}
            var Q12;
            {var subQ0=sQuery(id+"F44.wireOp",EDGE,"E71");var subQ1=sQuery(id+"F44.wireOp",EDGE,"E60.MirrorCS");var subQ2=makeQuery(id+"F44.imprint","INTERSECT",VERTEX,{"derivedFrom":[subQ1,subQ0]});Q12=makeQuery(id+"F44.imprint","IMPRINT",FACE,{"disambiguationData":[TD([[makeQuery(id+"F44.imprint","IMPRINT",EDGE,{"disambiguationData":[TD([[subQ2,-1.0]])],"derivedFrom":subQ1}),-1.0]])]});}
            var Q13;
            {var subQ5=sQuery(id+"F44.wireOp",EDGE,"E63.MirrorCS");Q13=makeQuery(id+"F44.imprint","IMPRINT",FACE,{"disambiguationData":[TD([[makeQuery(id+"F44.imprint","IMPRINT",EDGE,{"derivedFrom":subQ5}),1.0]])]});}
            extrude(context, id + "F45", {"entities" : qUnion([Q0, Q1, Q2, Q3, Q4, Q5, Q6, Q7, Q8, Q9, Q10, Q11, Q12, Q13]), "offsetDistance" : 25.4 * mm, "depth" : 2197.1 * mm, "hasSecondDirection" : true, "secondDirectionOppositeDirection" : false, "secondDirectionDepth" : 2082.8 * mm});
        }
        {
            var Q0;
            Q0=makeQuery(id+"F44.imprint","IMPRINT",FACE,{"disambiguationData":[TD([[makeQuery(id+"F44.imprint","IMPRINT",EDGE,{"derivedFrom":sQuery(id+"F44.wireOp",EDGE,"E67.MirrorCS")}),1.0]])]});
            var Q1;
            Q1=makeQuery(id+"F44.imprint","IMPRINT",FACE,{"disambiguationData":[TD([[makeQuery(id+"F44.imprint","IMPRINT",EDGE,{"derivedFrom":sQuery(id+"F44.wireOp",EDGE,"E56.bottom")}),1.0]])]});
            var Q2;
            Q2=makeQuery(id+"F44.imprint","IMPRINT",FACE,{"disambiguationData":[TD([[makeQuery(id+"F44.imprint","IMPRINT",EDGE,{"derivedFrom":sQuery(id+"F44.wireOp",EDGE,"E55.bottom")}),-1.0]])]});
            var Q3;
            Q3=makeQuery(id+"F44.imprint","IMPRINT",FACE,{"disambiguationData":[TD([[makeQuery(id+"F44.imprint","IMPRINT",EDGE,{"derivedFrom":sQuery(id+"F44.wireOp",EDGE,"E63.MirrorCS")}),-1.0]])]});
            extrude(context, id + "F46", {"entities" : qUnion([Q0, Q1, Q2, Q3]), "operationType" : NewBodyOperationType.ADD, "offsetDistance" : 25.4 * mm, "depth" : 2540 * mm});
        }
        {
            var Q0;
            {var subQ0=sQuery(id+"F44.wireOp",EDGE,"E72");var subQ1=sQuery(id+"F44.wireOp",EDGE,"E60.MirrorCS");var subQ2=makeQuery(id+"F44.imprint","INTERSECT",VERTEX,{"derivedFrom":[subQ1,subQ0]});Q0=makeQuery(id+"F44.imprint","IMPRINT",FACE,{"disambiguationData":[TD([[makeQuery(id+"F44.imprint","IMPRINT",EDGE,{"disambiguationData":[TD([[subQ2,-1.0]])],"derivedFrom":subQ1}),-1.0]])]});}
            var Q1;
            {var subQ0=sQuery(id+"F44.wireOp",EDGE,"E74");var subQ1=sQuery(id+"F44.wireOp",EDGE,"E58.right");var subQ2=makeQuery(id+"F44.imprint","INTERSECT",VERTEX,{"derivedFrom":[subQ1,subQ0]});Q1=makeQuery(id+"F44.imprint","IMPRINT",FACE,{"disambiguationData":[TD([[makeQuery(id+"F44.imprint","IMPRINT",EDGE,{"disambiguationData":[TD([[subQ2,1.0]])],"derivedFrom":subQ1}),-1.0]])]});}
            var Q2;
            {var subQ0=sQuery(id+"F44.wireOp",EDGE,"E71");var subQ1=sQuery(id+"F44.wireOp",EDGE,"E60.MirrorCS");var subQ2=makeQuery(id+"F44.imprint","INTERSECT",VERTEX,{"derivedFrom":[subQ1,subQ0]});Q2=makeQuery(id+"F44.imprint","IMPRINT",FACE,{"disambiguationData":[TD([[makeQuery(id+"F44.imprint","IMPRINT",EDGE,{"disambiguationData":[TD([[subQ2,-1.0]])],"derivedFrom":subQ1}),-1.0]])]});}
            var Q3;
            {var subQ0=sQuery(id+"F44.wireOp",EDGE,"E58.top");Q3=makeQuery(id+"F44.imprint","IMPRINT",FACE,{"disambiguationData":[TD([[makeQuery(id+"F44.imprint","IMPRINT",EDGE,{"derivedFrom":subQ0}),-1.0]])]});}
            var Q4;
            {var subQ0=sQuery(id+"F44.wireOp",EDGE,"E59.MirrorCS");Q4=makeQuery(id+"F44.imprint","IMPRINT",FACE,{"disambiguationData":[TD([[makeQuery(id+"F44.imprint","IMPRINT",EDGE,{"derivedFrom":subQ0}),1.0]])]});}
            var Q5;
            {var subQ0=sQuery(id+"F44.wireOp",EDGE,"E71");var subQ1=sQuery(id+"F44.wireOp",EDGE,"E58.left");var subQ2=makeQuery(id+"F44.imprint","INTERSECT",VERTEX,{"derivedFrom":[subQ1,subQ0]});Q5=makeQuery(id+"F44.imprint","IMPRINT",FACE,{"disambiguationData":[TD([[makeQuery(id+"F44.imprint","IMPRINT",EDGE,{"disambiguationData":[TD([[subQ2,-1.0]])],"derivedFrom":subQ1}),-1.0]])]});}
            var Q6;
            {var subQ0=sQuery(id+"F44.wireOp",EDGE,"E72");var subQ1=sQuery(id+"F44.wireOp",EDGE,"E58.left");var subQ2=makeQuery(id+"F44.imprint","INTERSECT",VERTEX,{"derivedFrom":[subQ1,subQ0]});Q6=makeQuery(id+"F44.imprint","IMPRINT",FACE,{"disambiguationData":[TD([[makeQuery(id+"F44.imprint","IMPRINT",EDGE,{"disambiguationData":[TD([[subQ2,-1.0]])],"derivedFrom":subQ1}),-1.0]])]});}
            var Q7;
            {var subQ0=sQuery(id+"F44.wireOp",EDGE,"E71");var subQ1=sQuery(id+"F44.wireOp",EDGE,"E58.right");var subQ2=makeQuery(id+"F44.imprint","INTERSECT",VERTEX,{"derivedFrom":[subQ1,subQ0]});Q7=makeQuery(id+"F44.imprint","IMPRINT",FACE,{"disambiguationData":[TD([[makeQuery(id+"F44.imprint","IMPRINT",EDGE,{"disambiguationData":[TD([[subQ2,-1.0]])],"derivedFrom":subQ1}),-1.0]])]});}
            var Q8;
            {var subQ0=sQuery(id+"F44.wireOp",EDGE,"E73");var subQ1=sQuery(id+"F44.wireOp",EDGE,"E58.left");var subQ2=makeQuery(id+"F44.imprint","INTERSECT",VERTEX,{"derivedFrom":[subQ1,subQ0]});Q8=makeQuery(id+"F44.imprint","IMPRINT",FACE,{"disambiguationData":[TD([[makeQuery(id+"F44.imprint","IMPRINT",EDGE,{"disambiguationData":[TD([[subQ2,-1.0]])],"derivedFrom":subQ1}),-1.0]])]});}
            var Q9;
            {var subQ0=sQuery(id+"F44.wireOp",EDGE,"E74");var subQ1=sQuery(id+"F44.wireOp",EDGE,"E60.MirrorCS");var subQ2=makeQuery(id+"F44.imprint","INTERSECT",VERTEX,{"derivedFrom":[subQ1,subQ0]});Q9=makeQuery(id+"F44.imprint","IMPRINT",FACE,{"disambiguationData":[TD([[makeQuery(id+"F44.imprint","IMPRINT",EDGE,{"disambiguationData":[TD([[subQ2,1.0]])],"derivedFrom":subQ1}),-1.0]])]});}
            var Q10;
            {var subQ0=sQuery(id+"F44.wireOp",EDGE,"E55.left");Q10=makeQuery(id+"F44.imprint","IMPRINT",FACE,{"disambiguationData":[TD([[makeQuery(id+"F44.imprint","IMPRINT",EDGE,{"derivedFrom":subQ0}),-1.0]])]});}
            var Q11;
            {var subQ0=sQuery(id+"F44.wireOp",EDGE,"E56.right");Q11=makeQuery(id+"F44.imprint","IMPRINT",FACE,{"disambiguationData":[TD([[makeQuery(id+"F44.imprint","IMPRINT",EDGE,{"derivedFrom":subQ0}),-1.0]])]});}
            var Q12;
            {var subQ5=sQuery(id+"F44.wireOp",EDGE,"E63.MirrorCS");Q12=makeQuery(id+"F44.imprint","IMPRINT",FACE,{"disambiguationData":[TD([[makeQuery(id+"F44.imprint","IMPRINT",EDGE,{"derivedFrom":subQ5}),1.0]])]});}
            var Q13;
            {var subQ5=sQuery(id+"F44.wireOp",EDGE,"E69.MirrorCS");Q13=makeQuery(id+"F44.imprint","IMPRINT",FACE,{"disambiguationData":[TD([[makeQuery(id+"F44.imprint","IMPRINT",EDGE,{"derivedFrom":subQ5}),1.0]])]});}
            extrude(context, id + "F47", {"entities" : qUnion([Q0, Q1, Q2, Q3, Q4, Q5, Q6, Q7, Q8, Q9, Q10, Q11, Q12, Q13]), "operationType" : NewBodyOperationType.ADD, "depth" : 114.3 * mm, "offsetDistance" : 25.4 * mm});
        }
    });
